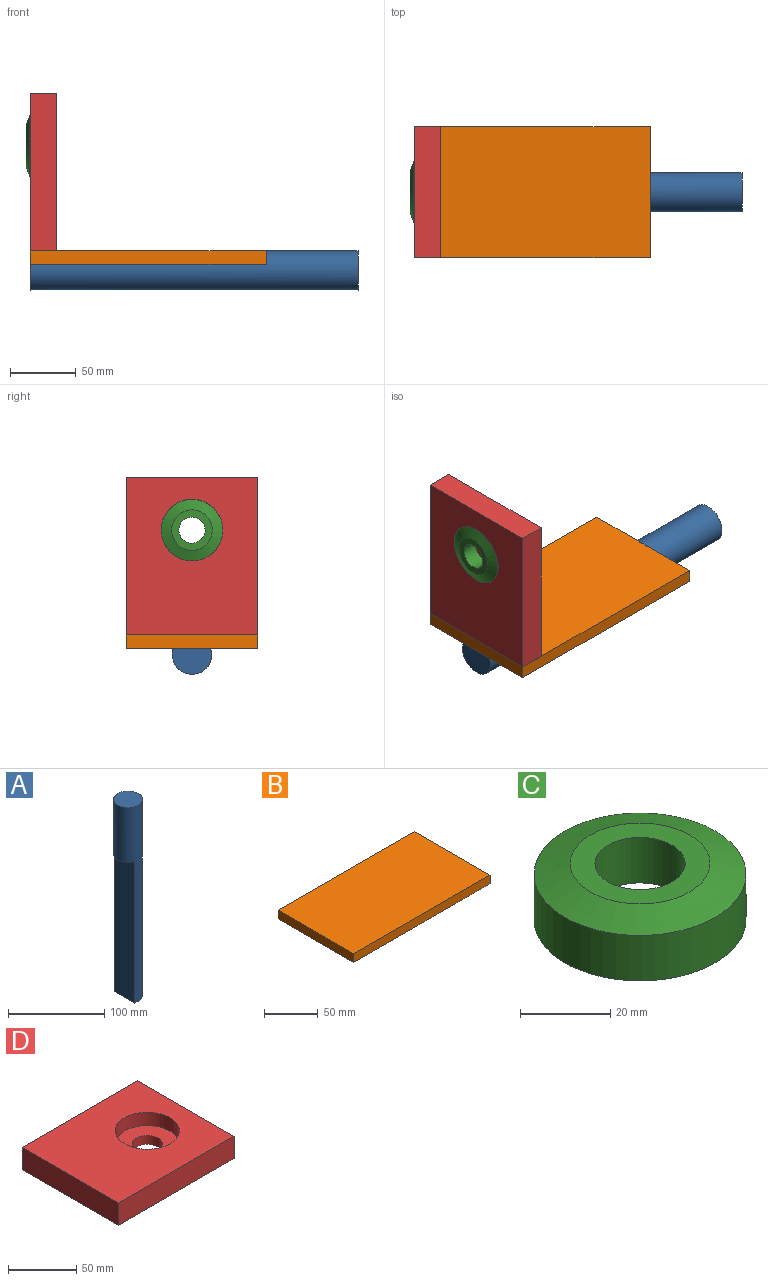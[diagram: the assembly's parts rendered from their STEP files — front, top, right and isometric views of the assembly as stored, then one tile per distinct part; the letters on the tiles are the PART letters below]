
ASSEMBLY  parts=4 mates=4
PART A: 5 faces, bbox 30x30x250 mm
  f0: plane 30x20mm, normal (0,0,-1), area 500.6mm2, adj f1,f4
  f1: cylinder r=15mm len=250mm, axis (0,0,-1), area 16914.8mm2, adj f0,f2,f3,f4
  f2: plane 30x30mm, normal (0,0,1), area 706.9mm2, adj f1
  f3: plane 28.28x10mm, normal (0,0,-1), area 206.3mm2, adj f1,f4
  f4: plane 180x28.28mm, normal (-1,0,0), area 5091.2mm2, adj f0,f1,f3
PART B: 6 faces, bbox 180x100x10 mm
  f0: plane 180x10mm, normal (0,1,0), area 1800mm2, adj f1,f3,f4,f5
  f1: plane 100x10mm, normal (-1,0,0), area 1000mm2, adj f0,f2,f4,f5
  f2: plane 180x10mm, normal (0,-1,0), area 1800mm2, adj f1,f3,f4,f5
  f3: plane 100x10mm, normal (1,0,0), area 1000mm2, adj f0,f2,f4,f5
  f4: plane 180x100mm, normal (0,0,1), area 18000mm2, adj f0,f1,f2,f3
  f5: plane 180x100mm, normal (0,0,-1), area 18000mm2, adj f0,f1,f2,f3
PART C: 6 faces, bbox 47x47x15.3 mm
  f0: cylinder r=10mm len=20mm, axis (0,0,-1), area 775.2mm2, adj f2,f4
  f1: cylinder r=23.5mm len=47mm, axis (0,0,-1), area 1821.8mm2, adj f3,f5
  f2: plane 31x31mm, normal (0,0,1), area 440.6mm2, adj f0,f5
  f3: plane 47x47mm, normal (0,0,-1), area 717.1mm2, adj f1,f4
  f4: cone r=18mm half-angle=70deg, axis (0,0,-1), area 748.9mm2, adj f0,f3
  f5: cone r=15.5mm half-angle=70deg, axis (0,0,-1), area 1043.1mm2, adj f1,f2
PART D: 9 faces, bbox 120x100x20 mm
  f0: plane 120x20mm, normal (0,1,0), area 2400mm2, adj f1,f3,f4,f5
  f1: plane 100x20mm, normal (-1,0,0), area 2000mm2, adj f0,f2,f4,f5
  f2: plane 120x20mm, normal (0,-1,0), area 2400mm2, adj f1,f3,f4,f5
  f3: plane 100x20mm, normal (1,0,0), area 2000mm2, adj f0,f2,f4,f5
  f4: plane 120x100mm, normal (0,0,1), area 10265.1mm2, adj f0,f1,f2,f3,f6
  f5: plane 120x100mm, normal (0,0,-1), area 11619.9mm2, adj f0,f1,f2,f3,f8
  f6: cylinder r=23.5mm len=47mm, axis (0,0,1), area 1771.9mm2, adj f4,f7
  f7: plane 47x47mm, normal (0,0,1), area 1354.8mm2, adj f6,f8
  f8: cylinder r=11mm len=22mm, axis (0,0,1), area 552.9mm2, adj f5,f7
PLACE A rot(axis=(0,1,0),90deg) t=(-333.33,-45.03,55.21)mm
PLACE B t=(-243.33,-45.03,60.21)mm
PLACE C rot(axis=(-0.7,-0.14,0.7),164.2deg) t=(-321.33,-45.03,150.21)mm
PLACE D rot(axis=(0,-1,0),90deg) t=(-313.33,-45.03,130.21)mm
MATE fastened A.f3 <-> B.f3  axis (-1,0,0) through (-153.33,-45.03,60.21)mm
MATE planar D.f6 <-> C.f1  axis (-1,0,0) through (-321.33,-45.03,150.21)mm
MATE cylindrical D.f6 <-> C.f0  axis (-1,0,0) through (-333.33,-45.03,150.21)mm
MATE fastened D.f1 <-> B.f4  axis (0,0,-1) through (-333.33,-45.03,70.21)mm
